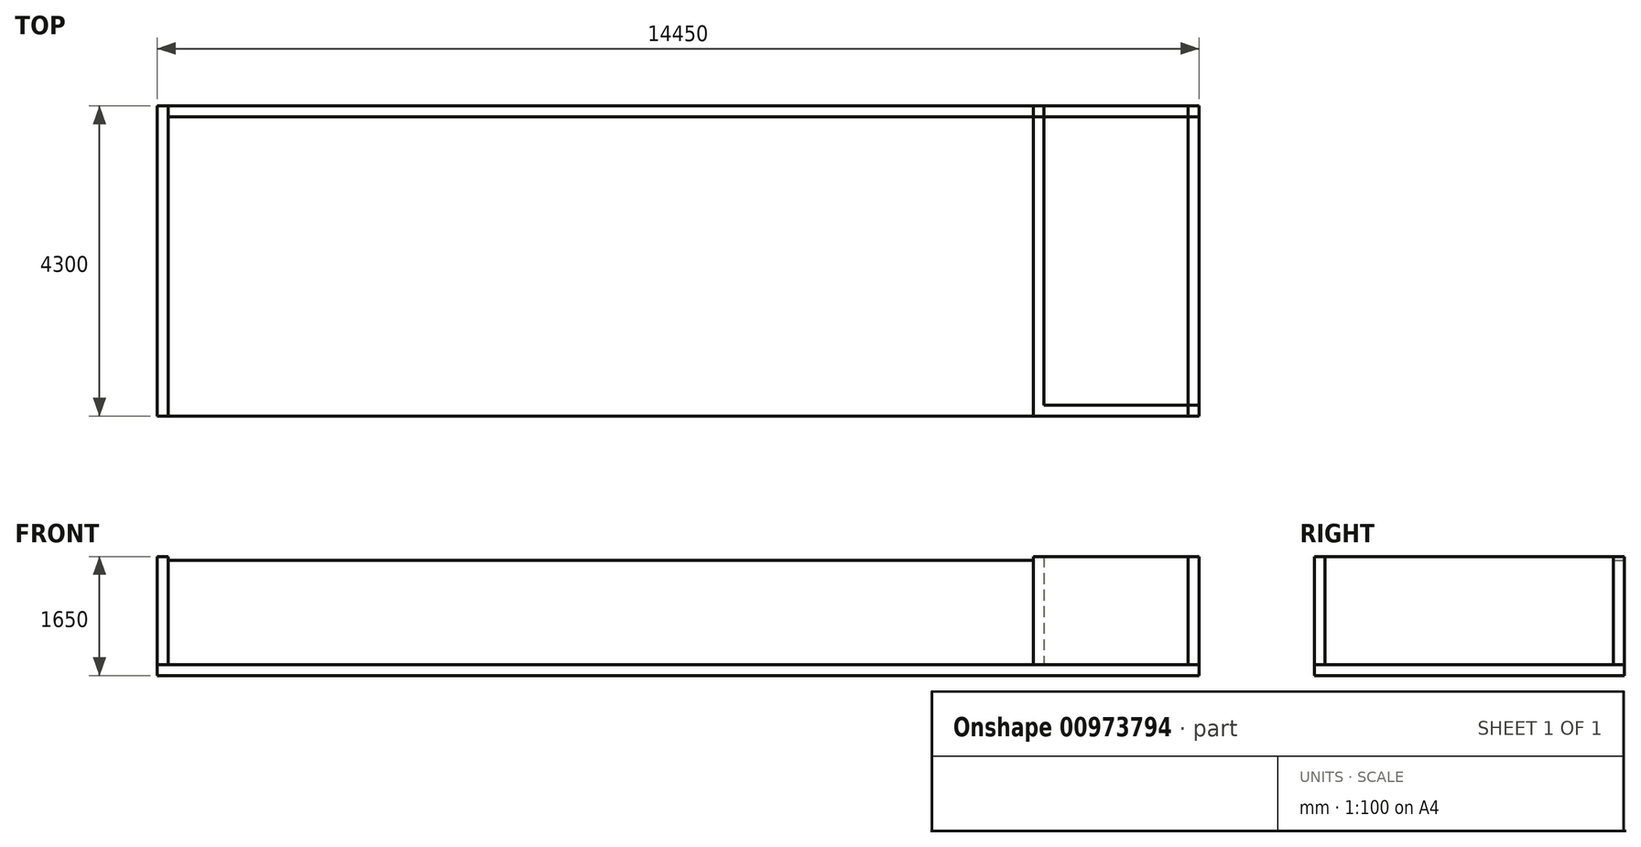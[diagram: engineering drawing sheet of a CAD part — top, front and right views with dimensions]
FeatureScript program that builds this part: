
annotation { "Feature Type Name" : "Feature", "Feature Type Description" : "" }
export const myFeature = defineFeature(function(context is Context, id is Id, definition is map)
    precondition{}
    {
        {
            var Q0;
            Q0=qCreatedBy(makeId("Top.planeOp"),FACE);
            var sketch = newSketch(context, id + "F0", { "sketchPlane" : qUnion([Q0])});
            skLineSegment(sketch, "E0.bottom", {"start": v(7225, -2150) * mm, "end": v(-7225, -2150) * mm});
            skLineSegment(sketch, "E0.top", {"start": v(7225, 2150) * mm, "end": v(-7225, 2150) * mm});
            skLineSegment(sketch, "E0.left", {"start": v(7225, -2150) * mm, "end": v(7225, 2150) * mm});
            skLineSegment(sketch, "E0.right", {"start": v(-7225, -2150) * mm, "end": v(-7225, 2150) * mm});
            skPoint(sketch, "E0.middle", {"position": v(0, 0) * mm});
            skSolve(sketch);
        }
        {
            var Q0;
            Q0 = qSketchRegion(id + "F0", true);
            extrude(context, id + "F1", {"entities" : qUnion([Q0]), "oppositeDirection" : true, "depth" : 150 * mm, "offsetDistance" : 25 * mm});
        }
        {
            var Q0;
            Q0=makeQuery(id+"F1.opExtrude","CAP_FACE",FACE,{"disambiguationData":[OSD([sQuery(id+"F0.wireOp",EDGE,"E0.bottom"),sQuery(id+"F0.wireOp",EDGE,"E0.top"),sQuery(id+"F0.wireOp",EDGE,"E0.left"),sQuery(id+"F0.wireOp",EDGE,"E0.right")])],"isStart":true});
            var sketch = newSketch(context, id + "F2", { "sketchPlane" : qUnion([Q0])});
            skLineSegment(sketch, "E1.bottom", {"start": v(-7225, 2150) * mm, "end": v(-7075, 2150) * mm});
            skLineSegment(sketch, "E1.top", {"start": v(-7225, -2150) * mm, "end": v(-7075, -2150) * mm});
            skLineSegment(sketch, "E1.left", {"start": v(-7225, 2150) * mm, "end": v(-7225, -2150) * mm});
            skLineSegment(sketch, "E1.right", {"start": v(-7075, 2150) * mm, "end": v(-7075, -2150) * mm});
            skLineSegment(sketch, "E2.bottom", {"start": v(-7075, 2150) * mm, "end": v(4925, 2150) * mm});
            skLineSegment(sketch, "E2.top", {"start": v(-7075, 2000) * mm, "end": v(4925, 2000) * mm});
            skLineSegment(sketch, "E2.left", {"start": v(-7075, 2150) * mm, "end": v(-7075, 2000) * mm});
            skLineSegment(sketch, "E2.right", {"start": v(4925, 2150) * mm, "end": v(4925, 2000) * mm});
            skLineSegment(sketch, "E3.bottom", {"start": v(4925, 2150) * mm, "end": v(5075, 2150) * mm});
            skLineSegment(sketch, "E3.top", {"start": v(4925, -2150) * mm, "end": v(5075, -2150) * mm});
            skLineSegment(sketch, "E3.left", {"start": v(4925, 2150) * mm, "end": v(4925, -2150) * mm});
            skLineSegment(sketch, "E3.right", {"start": v(5075, 2150) * mm, "end": v(5075, -2150) * mm});
            skLineSegment(sketch, "E4.bottom", {"start": v(-7075, -2150) * mm, "end": v(7225, -2150) * mm});
            skLineSegment(sketch, "E4.top", {"start": v(-7075, -2000) * mm, "end": v(7225, -2000) * mm});
            skLineSegment(sketch, "E4.left", {"start": v(-7075, -2150) * mm, "end": v(-7075, -2000) * mm});
            skLineSegment(sketch, "E4.right", {"start": v(7225, -2150) * mm, "end": v(7225, -2000) * mm});
            skLineSegment(sketch, "E5.bottom", {"start": v(7225, -2150) * mm, "end": v(7075, -2150) * mm});
            skLineSegment(sketch, "E5.top", {"start": v(7225, 2150) * mm, "end": v(7075, 2150) * mm});
            skLineSegment(sketch, "E5.left", {"start": v(7225, -2150) * mm, "end": v(7225, 2150) * mm});
            skLineSegment(sketch, "E5.right", {"start": v(7075, -2150) * mm, "end": v(7075, 2150) * mm});
            skLineSegment(sketch, "E6.bottom", {"start": v(4925, 2000) * mm, "end": v(7225, 2000) * mm});
            skLineSegment(sketch, "E6.top", {"start": v(4925, 2150) * mm, "end": v(7225, 2150) * mm});
            skLineSegment(sketch, "E6.left", {"start": v(4925, 2000) * mm, "end": v(4925, 2150) * mm});
            skLineSegment(sketch, "E6.right", {"start": v(7225, 2000) * mm, "end": v(7225, 2150) * mm});
            skSolve(sketch);
        }
        {
            var Q0;
            Q0=makeQuery(id+"F2.imprint","IMPRINT",FACE,{"disambiguationData":[TD([[makeQuery(id+"F2.imprint","IMPRINT",EDGE,{"derivedFrom":sQuery(id+"F2.wireOp",EDGE,"E1.bottom")}),1.0]])]});
            var Q1;
            Q1=makeQuery(id+"F2.imprint","IMPRINT",FACE,{"disambiguationData":[TD([[makeQuery(id+"F2.imprint","IMPRINT",EDGE,{"derivedFrom":sQuery(id+"F2.wireOp",EDGE,"E2.bottom")}),1.0]])]});
            var Q2;
            {var subQ5=sQuery(id+"F2.wireOp",EDGE,"E4.left");Q2=makeQuery(id+"F2.imprint","IMPRINT",FACE,{"disambiguationData":[TD([[makeQuery(id+"F2.imprint","IMPRINT",EDGE,{"derivedFrom":subQ5}),-1.0]])]});}
            var Q3;
            {var subQ0=sQuery(id+"F2.wireOp",EDGE,"E6.bottom");var subQ5=sQuery(id+"F2.wireOp",EDGE,"E3.right");var subQ6=makeQuery(id+"F2.imprint","INTERSECT",VERTEX,{"derivedFrom":[subQ5,subQ0]});Q3=makeQuery(id+"F2.imprint","IMPRINT",FACE,{"disambiguationData":[TD([[makeQuery(id+"F2.imprint","IMPRINT",EDGE,{"disambiguationData":[TD([[subQ6,-1.0]])],"derivedFrom":subQ5}),-1.0]])]});}
            var Q4;
            {var subQ5=sQuery(id+"F2.wireOp",EDGE,"E6.left");Q4=makeQuery(id+"F2.imprint","IMPRINT",FACE,{"disambiguationData":[TD([[makeQuery(id+"F2.imprint","IMPRINT",EDGE,{"derivedFrom":subQ5}),-1.0]])]});}
            var Q5;
            {var subQ0=sQuery(id+"F2.wireOp",EDGE,"E6.top");var subQ1=sQuery(id+"F2.wireOp",EDGE,"E3.right");var subQ2=makeQuery(id+"F2.imprint","INTERSECT",VERTEX,{"derivedFrom":[subQ1,subQ0]});Q5=makeQuery(id+"F2.imprint","IMPRINT",FACE,{"disambiguationData":[TD([[makeQuery(id+"F2.imprint","IMPRINT",EDGE,{"disambiguationData":[TD([[subQ2,-1.0]])],"derivedFrom":subQ1}),1.0]])]});}
            var Q6;
            {var subQ0=sQuery(id+"F2.wireOp",EDGE,"E5.left");var subQ1=sQuery(id+"F2.wireOp",EDGE,"E4.top");var subQ2=makeQuery(id+"F2.imprint","INTERSECT",VERTEX,{"derivedFrom":[subQ1,subQ0]});Q6=makeQuery(id+"F2.imprint","IMPRINT",FACE,{"disambiguationData":[TD([[makeQuery(id+"F2.imprint","IMPRINT",EDGE,{"disambiguationData":[TD([[subQ2,1.0]])],"derivedFrom":subQ1}),1.0]])]});}
            var Q7;
            {var subQ5=sQuery(id+"F2.wireOp",EDGE,"E6.right");Q7=makeQuery(id+"F2.imprint","IMPRINT",FACE,{"disambiguationData":[TD([[makeQuery(id+"F2.imprint","IMPRINT",EDGE,{"derivedFrom":subQ5}),1.0]])]});}
            var Q8;
            {var subQ5=sQuery(id+"F2.wireOp",EDGE,"E5.bottom");Q8=makeQuery(id+"F2.imprint","IMPRINT",FACE,{"disambiguationData":[TD([[makeQuery(id+"F2.imprint","IMPRINT",EDGE,{"derivedFrom":subQ5}),-1.0]])]});}
            var Q9;
            {var subQ0=sQuery(id+"F2.wireOp",EDGE,"E4.bottom");var subQ1=sQuery(id+"F2.wireOp",EDGE,"E3.right");var subQ2=makeQuery(id+"F2.imprint","INTERSECT",VERTEX,{"derivedFrom":[subQ1,subQ0]});Q9=makeQuery(id+"F2.imprint","IMPRINT",FACE,{"disambiguationData":[TD([[makeQuery(id+"F2.imprint","IMPRINT",EDGE,{"disambiguationData":[TD([[subQ2,1.0]])],"derivedFrom":subQ1}),1.0]])]});}
            var Q10;
            {var subQ0=sQuery(id+"F2.wireOp",EDGE,"E4.bottom");var subQ1=sQuery(id+"F2.wireOp",EDGE,"E3.left");var subQ2=makeQuery(id+"F2.imprint","INTERSECT",VERTEX,{"derivedFrom":[subQ1,subQ0]});Q10=makeQuery(id+"F2.imprint","IMPRINT",FACE,{"disambiguationData":[TD([[makeQuery(id+"F2.imprint","IMPRINT",EDGE,{"disambiguationData":[TD([[subQ2,1.0]])],"derivedFrom":subQ1}),1.0]])]});}
            extrude(context, id + "F3", {"entities" : qUnion([Q0, Q1, Q2, Q3, Q4, Q5, Q6, Q7, Q8, Q9, Q10]), "depth" : 1500 * mm, "offsetDistance" : 25 * mm});
        }
        {
            var Q0;
            Q0=makeQuery(id+"F3.opExtrude","CAP_FACE",FACE,{"disambiguationData":[OSD([sQuery(id+"F2.wireOp",EDGE,"E1.bottom"),sQuery(id+"F2.wireOp",EDGE,"E1.top"),sQuery(id+"F2.wireOp",EDGE,"E1.left"),sQuery(id+"F2.wireOp",EDGE,"E1.right"),sQuery(id+"F2.wireOp",EDGE,"E2.bottom"),sQuery(id+"F2.wireOp",EDGE,"E2.top"),sQuery(id+"F2.wireOp",EDGE,"E3.left"),sQuery(id+"F2.wireOp",EDGE,"E3.right"),sQuery(id+"F2.wireOp",EDGE,"E4.bottom"),sQuery(id+"F2.wireOp",EDGE,"E4.top"),sQuery(id+"F2.wireOp",EDGE,"E5.bottom"),sQuery(id+"F2.wireOp",EDGE,"E5.left"),sQuery(id+"F2.wireOp",EDGE,"E5.right"),sQuery(id+"F2.wireOp",EDGE,"E6.bottom"),sQuery(id+"F2.wireOp",EDGE,"E6.top"),sQuery(id+"F2.wireOp",EDGE,"E6.right")])],"isStart":false});
            var sketch = newSketch(context, id + "F4", { "sketchPlane" : qUnion([Q0])});
            skLineSegment(sketch, "E7.bottom", {"start": v(-7075, 2000) * mm, "end": v(4925, 2000) * mm});
            skLineSegment(sketch, "E7.top", {"start": v(-7075, 2150) * mm, "end": v(4925, 2150) * mm});
            skLineSegment(sketch, "E7.left", {"start": v(-7075, 2000) * mm, "end": v(-7075, 2150) * mm});
            skLineSegment(sketch, "E7.right", {"start": v(4925, 2000) * mm, "end": v(4925, 2150) * mm});
            skSolve(sketch);
        }
        {
            var Q0;
            Q0 = qSketchRegion(id + "F4", true);
            extrude(context, id + "F5", {"entities" : qUnion([Q0]), "operationType" : NewBodyOperationType.REMOVE, "oppositeDirection" : true, "depth" : 50 * mm, "offsetDistance" : 25 * mm});
        }
    });
